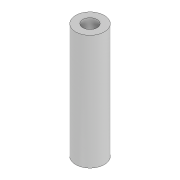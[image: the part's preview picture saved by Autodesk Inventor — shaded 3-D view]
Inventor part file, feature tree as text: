
AUTODESK INVENTOR PART (.ipt)
format: ipt  version: 2022 (Build 260153000, 153)  size: 89,088 bytes
history: native  units: mm
features: extrude x2, sketch x2
ambient origin geometry x8: Origin, YZ Plane, XZ Plane, XY Plane, X Axis, Y Axis, Z Axis, Center Point
bodies: Solid1 (feature_tree)
feature tree (4):
  extrude  "Extrusion1"  Depth=40.0mm TaperAngle=0.0deg
  extrude  "Extrusion2"  Depth=40.0mm TaperAngle=0.0deg
  sketch  "Sketch1"  dims[d0=10.0mm d1=40.0mm d2=0.0mm]
  sketch  "Sketch2"  dims[d3=5.0mm d4=40.0mm d5=0.0mm]
